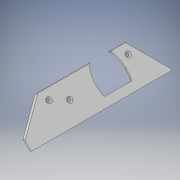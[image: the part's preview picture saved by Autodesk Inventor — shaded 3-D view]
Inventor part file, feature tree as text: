
AUTODESK INVENTOR PART (.ipt)
format: ipt  version: 2019 (Build 230136000, 136)  size: 179,200 bytes
history: native  units: mm
features: extrude x5, sketch x5, chamfer x3, other x1
ambient origin geometry x8: Origin, YZ Plane, XZ Plane, XY Plane, X Axis, Y Axis, Z Axis, Center Point
bodies: Body1 (feature_tree)
feature tree (14):
  other  "Bryła1"
  extrude  "Wyciągnięcie proste1"  Depth=2.0mm
  extrude  "Wyciągnięcie proste2"  Depth=30.0mm
  extrude  "Wyciągnięcie proste3"  TaperAngle=45.0deg  [1 undecoded]
  chamfer  "Faza1"  Distance=2.0mm
  chamfer  "Faza2"  Distance=180.257mm
  chamfer  "Faza3"  Angle=45.0deg  [1 undecoded]
  extrude  "Wyciągnięcie proste4"  TaperAngle=30.0deg  [1 undecoded]
  extrude  "Wyciągnięcie proste5"  Depth=22.0mm
  sketch  "Szkic1"
  sketch  "Szkic2"
  sketch  "Szkic3"
  sketch  "Szkic4"
  sketch  "Szkic5"
note: 3 required parameter values undecoded (feature->parameter linkage not recoverable at this tier; creation-order binding heuristic only, values carry confidence <= 0.55)
